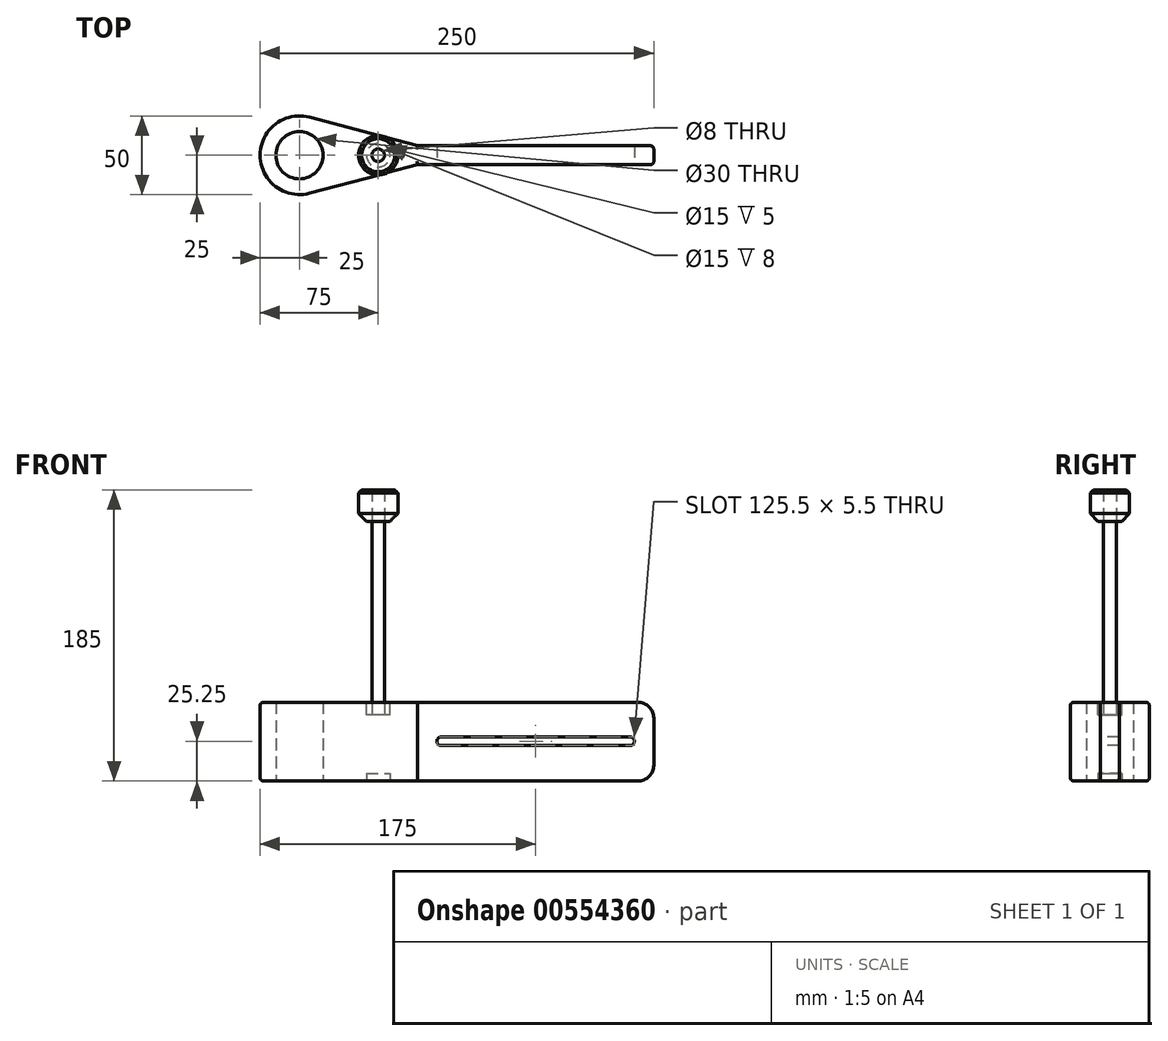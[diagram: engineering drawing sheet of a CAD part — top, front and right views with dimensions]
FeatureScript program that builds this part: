
annotation { "Feature Type Name" : "Feature", "Feature Type Description" : "" }
export const myFeature = defineFeature(function(context is Context, id is Id, definition is map)
    precondition{}
    {
        {
            var Q0;
            Q0=qCreatedBy(makeId("Top.planeOp"),FACE);
            var sketch = newSketch(context, id + "F0", { "sketchPlane" : qUnion([Q0])});
            skCircle(sketch, "E0", {"center": v(0, 0) * mm, "radius": 15 * mm});
            skLineSegment(sketch, "E1", {"start": v(0, 0) * mm, "end": v(50, 0) * mm});
            skCircle(sketch, "E2", {"center": v(50, 0) * mm, "radius": 4 * mm});
            skLineSegment(sketch, "E3", {"start": v(75, 6) * mm, "end": v(225, 6) * mm});
            skLineSegment(sketch, "E4", {"start": v(225, -6) * mm, "end": v(75, -6) * mm});
            skLineSegment(sketch, "E5", {"start": v(0, 0) * mm, "end": v(75, 0) * mm, "construction": true});
            skLineSegment(sketch, "E6", {"start": v(75, 0) * mm, "end": v(75, 6) * mm, "construction": true});
            skLineSegment(sketch, "E7", {"start": v(225, 6) * mm, "end": v(225, 0) * mm});
            skLineSegment(sketch, "E8", {"start": v(225, -6) * mm, "end": v(225, 0) * mm});
            skArc(sketch, "E9", {"start": v(6.4, 24.17) * mm, "mid": v(-25, 0) * mm, "end": v(6.4, -24.17) * mm});
            skLineSegment(sketch, "E10", {"start": v(75, 6) * mm, "end": v(6.4, 24.17) * mm});
            skLineSegment(sketch, "E11", {"start": v(75, -6) * mm, "end": v(6.4, -24.17) * mm});
            skSolve(sketch);
        }
        {
            var Q0;
            Q0 = qSketchRegion(id + "F0", true);
            extrude(context, id + "F1", {"entities" : qUnion([Q0]), "depth" : 50 * mm, "offsetDistance" : 25 * mm});
        }
        {
            var Q0;
            Q0=makeQuery(id+"F1.opExtrude","SWEPT_FACE",FACE,{"disambiguationData":[OSD([sQuery(id+"F0.wireOp",EDGE,"E4")])]});
            var sketch = newSketch(context, id + "F2", { "sketchPlane" : qUnion([Q0])});
            skLineSegment(sketch, "E12", {"start": v(90, 25.25) * mm, "end": v(210, 25.25) * mm, "construction": true});
            skLineSegment(sketch, "E13", {"start": v(150, 0) * mm, "end": v(150, 25.25) * mm});
            skArc(sketch, "E14.0.startCap", {"start": v(90, 22.5) * mm, "mid": v(87.25, 25.25) * mm, "end": v(90, 28) * mm});
            skArc(sketch, "E14.0.endCap", {"start": v(210, 28) * mm, "mid": v(212.75, 25.25) * mm, "end": v(210, 22.5) * mm});
            skLineSegment(sketch, "E14.0.left", {"start": v(90, 28) * mm, "end": v(210, 28) * mm});
            skLineSegment(sketch, "E14.0.right", {"start": v(90, 22.5) * mm, "end": v(210, 22.5) * mm});
            skSolve(sketch);
        }
        {
            var Q0;
            Q0 = qSketchRegion(id + "F2", true);
            extrude(context, id + "F3", {"entities" : qUnion([Q0]), "operationType" : NewBodyOperationType.REMOVE, "oppositeDirection" : true, "depth" : 25 * mm, "offsetDistance" : 25 * mm});
        }
        {
            var Q0;
            Q0=makeQuery(id+"F1.opExtrude","CAP_FACE",FACE,{"disambiguationData":[OSD([sQuery(id+"F0.wireOp",EDGE,"E0"),sQuery(id+"F0.wireOp",EDGE,"E2"),sQuery(id+"F0.wireOp",EDGE,"E3"),sQuery(id+"F0.wireOp",EDGE,"E4"),sQuery(id+"F0.wireOp",EDGE,"E7"),sQuery(id+"F0.wireOp",EDGE,"E8"),sQuery(id+"F0.wireOp",EDGE,"E9"),sQuery(id+"F0.wireOp",EDGE,"E10"),sQuery(id+"F0.wireOp",EDGE,"E11")])],"isStart":true});
            var sketch = newSketch(context, id + "F4", { "sketchPlane" : qUnion([Q0])});
            skCircle(sketch, "E15", {"center": v(50, 0) * mm, "radius": 7.5 * mm});
            skSolve(sketch);
        }
        {
            var Q0;
            Q0 = qSketchRegion(id + "F4", true);
            extrude(context, id + "F5", {"entities" : qUnion([Q0]), "operationType" : NewBodyOperationType.REMOVE, "oppositeDirection" : true, "depth" : 15 * mm, "offsetDistance" : 25 * mm});
        }
        {
            var Q0;
            Q0=makeQuery(id+"F1.opExtrude","CAP_FACE",FACE,{"disambiguationData":[OSD([sQuery(id+"F0.wireOp",EDGE,"E0"),sQuery(id+"F0.wireOp",EDGE,"E2"),sQuery(id+"F0.wireOp",EDGE,"E3"),sQuery(id+"F0.wireOp",EDGE,"E4"),sQuery(id+"F0.wireOp",EDGE,"E7"),sQuery(id+"F0.wireOp",EDGE,"E8"),sQuery(id+"F0.wireOp",EDGE,"E9"),sQuery(id+"F0.wireOp",EDGE,"E10"),sQuery(id+"F0.wireOp",EDGE,"E11")])],"isStart":false});
            var sketch = newSketch(context, id + "F6", { "sketchPlane" : qUnion([Q0])});
            skCircle(sketch, "E16", {"center": v(50, 0) * mm, "radius": 7.5 * mm});
            skSolve(sketch);
        }
        {
            var Q0;
            Q0 = qSketchRegion(id + "F6", true);
            extrude(context, id + "F7", {"entities" : qUnion([Q0]), "operationType" : NewBodyOperationType.REMOVE, "oppositeDirection" : true, "depth" : 8 * mm, "offsetDistance" : 25 * mm});
        }
        {
            var Q0;
            Q0=makeQuery(id+"F1.opExtrude","CAP_EDGE",EDGE,{"disambiguationData":[OSD([sQuery(id+"F0.wireOp",EDGE,"E7"),sQuery(id+"F0.wireOp",EDGE,"E8")])],"isStart":false});
            var Q1;
            Q1=makeQuery(id+"F1.opExtrude","CAP_EDGE",EDGE,{"disambiguationData":[OSD([sQuery(id+"F0.wireOp",EDGE,"E7"),sQuery(id+"F0.wireOp",EDGE,"E8")])],"isStart":true});
            fillet(context, id + "F8", {"entities" : qUnion([Q0, Q1]), "radius" : 10 * mm, "tangentPropagation" : true, "allowEdgeOverflow" : false});
        }
        {
            var Q0;
            Q0=makeQuery(id+"F1.opExtrude","CAP_EDGE",EDGE,{"disambiguationData":[OSD([sQuery(id+"F0.wireOp",EDGE,"E3")])],"isStart":false});
            var Q1;
            Q1=makeQuery(id+"F1.opExtrude","CAP_EDGE",EDGE,{"disambiguationData":[OSD([sQuery(id+"F0.wireOp",EDGE,"E4")])],"isStart":false});
            var Q2;
            Q2=makeQuery(id+"F1.opExtrude","CAP_EDGE",EDGE,{"disambiguationData":[OSD([sQuery(id+"F0.wireOp",EDGE,"E10")])],"isStart":false});
            var Q3;
            Q3=makeQuery(id+"F1.opExtrude","CAP_EDGE",EDGE,{"disambiguationData":[OSD([sQuery(id+"F0.wireOp",EDGE,"E10")])],"isStart":true});
            fillet(context, id + "F9", {"entities" : qUnion([Q0, Q1, Q2, Q3]), "radius" : 2 * mm, "tangentPropagation" : true, "allowEdgeOverflow" : false});
        }
        {
            var Q0;
            Q0 = qSketchRegion(id + "F2", true);
            extrude(context, id + "F10", {"entities" : qUnion([Q0]), "operationType" : NewBodyOperationType.REMOVE, "oppositeDirection" : true, "depth" : 25 * mm, "offsetDistance" : 25 * mm});
        }
        {
            var Q0;
            Q0=makeQuery(id+"F5.boolean.opBoolean","COPY",FACE,{"derivedFrom":makeQuery(id+"F5.opExtrude","CAP_FACE",FACE,{"disambiguationData":[OSD([sQuery(id+"F4.wireOp",EDGE,"E15")])],"isStart":false})});
            var sketch = newSketch(context, id + "F11", { "sketchPlane" : qUnion([Q0])});
            skCircle(sketch, "E17", {"center": v(50, 0) * mm, "radius": 7.5 * mm});
            skSolve(sketch);
        }
        {
            var Q0;
            Q0 = qSketchRegion(id + "F11", true);
            extrude(context, id + "F12", {"entities" : qUnion([Q0]), "depth" : 10 * mm, "offsetDistance" : 25 * mm});
        }
        {
            var Q0;
            Q0=makeQuery(id+"F12.opExtrude","CAP_FACE",FACE,{"disambiguationData":[OSD([sQuery(id+"F11.wireOp",EDGE,"E17")])],"isStart":true});
            var sketch = newSketch(context, id + "F13", { "sketchPlane" : qUnion([Q0])});
            skCircle(sketch, "E18", {"center": v(50, 0) * mm, "radius": 4 * mm});
            skSolve(sketch);
        }
        {
            var Q0;
            Q0 = qSketchRegion(id + "F13", true);
            extrude(context, id + "F14", {"entities" : qUnion([Q0]), "operationType" : NewBodyOperationType.ADD, "depth" : 150 * mm, "offsetDistance" : 25 * mm});
        }
        {
            var Q0;
            Q0=makeQuery(id+"F14.opExtrude","CAP_FACE",FACE,{"disambiguationData":[OSD([sQuery(id+"F13.wireOp",EDGE,"E18")])],"isStart":false});
            var sketch = newSketch(context, id + "F15", { "sketchPlane" : qUnion([Q0])});
            skCircle(sketch, "E19", {"center": v(50, 0) * mm, "radius": 4 * mm});
            skCircle(sketch, "E20", {"center": v(50, 0) * mm, "radius": 12.5 * mm});
            skSolve(sketch);
        }
        {
            var Q0;
            Q0 = qSketchRegion(id + "F15", true);
            extrude(context, id + "F16", {"entities" : qUnion([Q0]), "depth" : 20 * mm, "offsetDistance" : 25 * mm});
        }
        {
            var Q0;
            Q0=makeQuery(id+"F16.opExtrude","CAP_EDGE",EDGE,{"disambiguationData":[OSD([sQuery(id+"F15.wireOp",EDGE,"E20")])],"isStart":false});
            chamfer(context, id + "F17", {"entities" : qUnion([Q0]), "width" : 2 * mm, "tangentPropagation" : true});
        }
        {
            var Q0;
            Q0=makeQuery(id+"F16.opExtrude","CAP_EDGE",EDGE,{"disambiguationData":[OSD([sQuery(id+"F15.wireOp",EDGE,"E20")])],"isStart":true});
            chamfer(context, id + "F18", {"entities" : qUnion([Q0]), "width" : 5 * mm, "tangentPropagation" : true});
        }
    });
